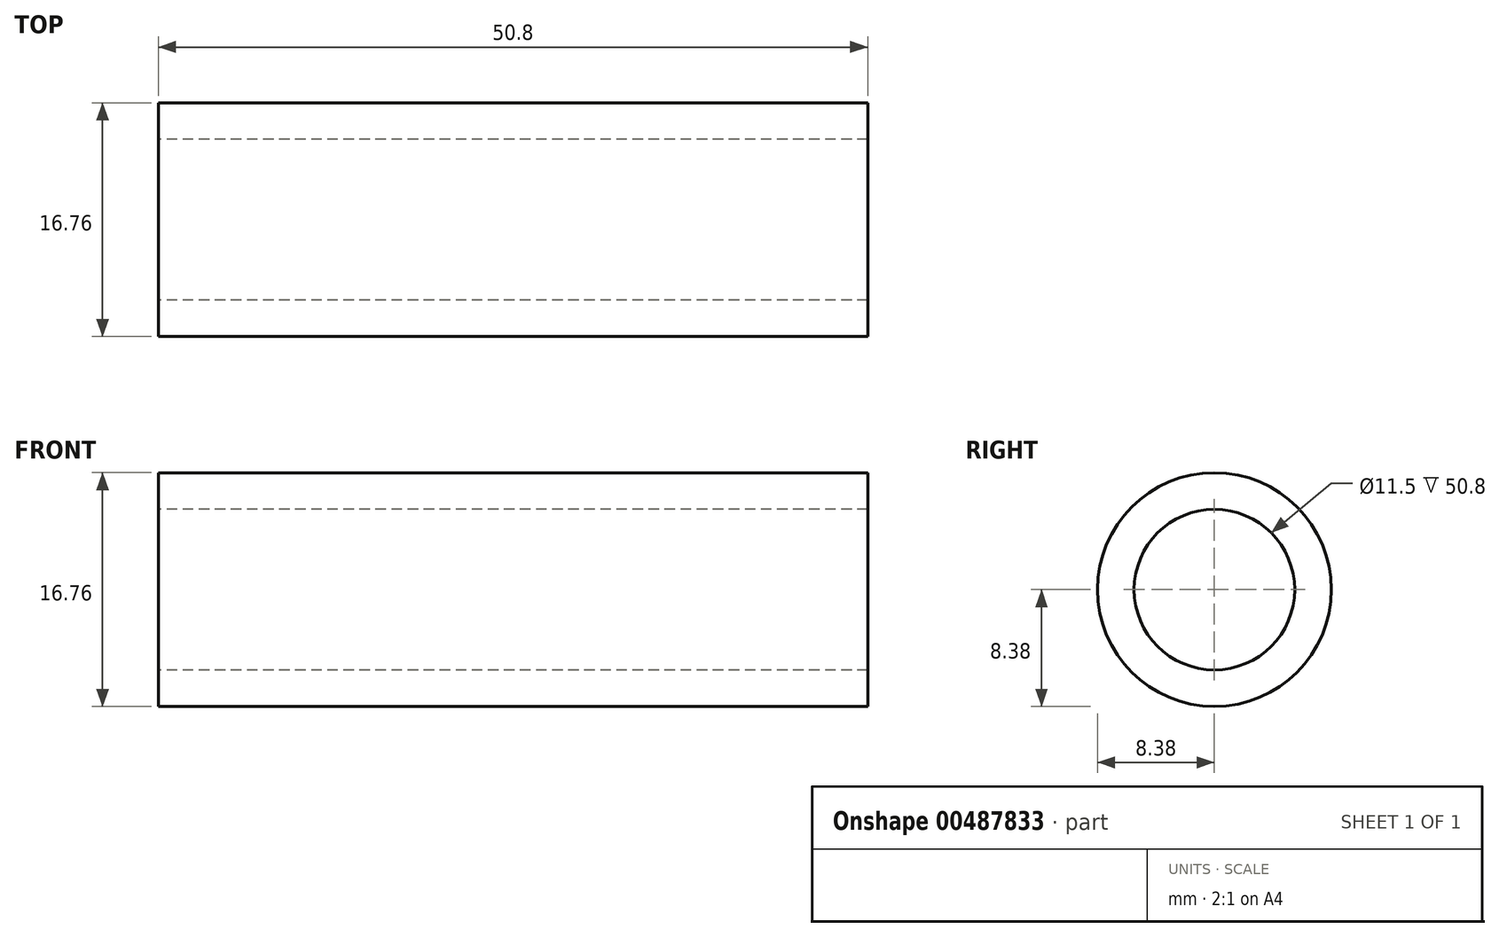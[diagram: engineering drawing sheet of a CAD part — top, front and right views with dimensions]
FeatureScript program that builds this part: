
annotation { "Feature Type Name" : "Feature", "Feature Type Description" : "" }
export const myFeature = defineFeature(function(context is Context, id is Id, definition is map)
    precondition{}
    {
        {
            var Q0;
            Q0=qCreatedBy(makeId("Right.planeOp"),FACE);
            var sketch = newSketch(context, id + "F0", { "sketchPlane" : qUnion([Q0])});
            skCircle(sketch, "E0", {"center": v(0, 0) * mm, "radius": 8.35 * mm});
            skCircle(sketch, "E1", {"center": v(0, 0) * mm, "radius": 8.38 * mm});
            skCircle(sketch, "E2", {"center": v(0, 0) * mm, "radius": 5.75 * mm});
            skSolve(sketch);
        }
        {
            var Q0;
            Q0=makeQuery(id+"F0.imprint","IMPRINT",FACE,{"disambiguationData":[TD([[makeQuery(id+"F0.imprint","IMPRINT",EDGE,{"derivedFrom":sQuery(id+"F0.wireOp",EDGE,"E0")}),1.0]])]});
            var Q1;
            Q1=makeQuery(id+"F0.imprint","IMPRINT",FACE,{"disambiguationData":[TD([[makeQuery(id+"F0.imprint","IMPRINT",EDGE,{"derivedFrom":sQuery(id+"F0.wireOp",EDGE,"E0")}),-1.0]])]});
            extrude(context, id + "F1", {"entities" : qUnion([Q0, Q1]), "depth" : 25.4 * mm});
        }
        {
            var Q0;
            Q0 = qSketchRegion(id + "F0", true);
            var Q1;
            Q1=makeQuery(id+"F1.opExtrude","CAP_FACE",FACE,{"disambiguationData":[OSD([sQuery(id+"F0.wireOp",EDGE,"E1"),sQuery(id+"F0.wireOp",EDGE,"E2")])],"isStart":false});
            extrude(context, id + "F2", {"entities" : qUnion([Q0, Q1]), "operationType" : NewBodyOperationType.ADD, "depth" : 25.4 * mm});
        }
    });
